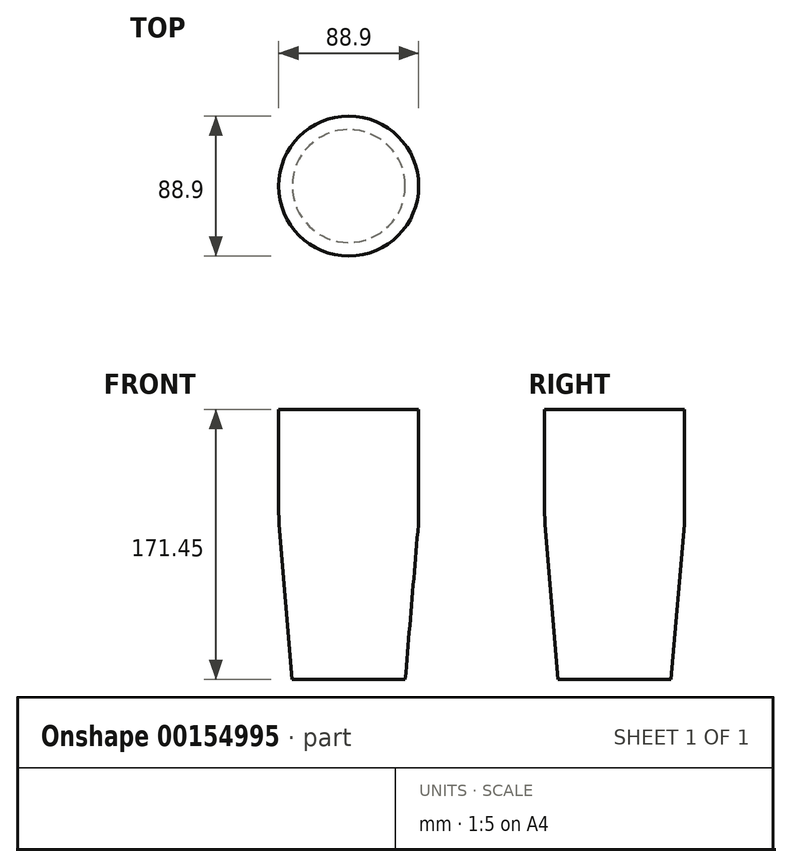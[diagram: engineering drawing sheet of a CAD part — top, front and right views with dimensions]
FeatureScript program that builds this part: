
annotation { "Feature Type Name" : "Feature", "Feature Type Description" : "" }
export const myFeature = defineFeature(function(context is Context, id is Id, definition is map)
    precondition{}
    {
        {
            var Q0;
            Q0=qCreatedBy(makeId("Front.planeOp"),FACE);
            var sketch = newSketch(context, id + "F0", { "sketchPlane" : qUnion([Q0])});
            skLineSegment(sketch, "E0", {"start": v(0, 0) * mm, "end": v(35.88, 0) * mm});
            skLineSegment(sketch, "E1", {"start": v(35.88, 0) * mm, "end": v(44.18, 98.4) * mm});
            skLineSegment(sketch, "E2", {"start": v(44.45, 104.8) * mm, "end": v(44.45, 171.45) * mm});
            skLineSegment(sketch, "E3", {"start": v(44.45, 171.45) * mm, "end": v(0, 171.45) * mm});
            skLineSegment(sketch, "E4", {"start": v(0, 171.45) * mm, "end": v(0, 0) * mm});
            skPoint(sketch, "E5.visualSharp", {"position": v(44.45, 101.6) * mm});
            skArc(sketch, "E5.filletArc", {"start": v(44.18, 98.4) * mm, "mid": v(44.38, 101.6) * mm, "end": v(44.45, 104.8) * mm});
            skSolve(sketch);
        }
        {
            var Q0;
            Q0 = qSketchRegion(id + "F0", true);
            var Q1;
            Q1=sQuery(id+"F0.wireOp",EDGE,"E4");
            revolve(context, id + "F1", {"entities" : qUnion([Q0]), "axis" : qUnion([Q1]), "revolveType" : RevolveType.FULL});
        }
    });
